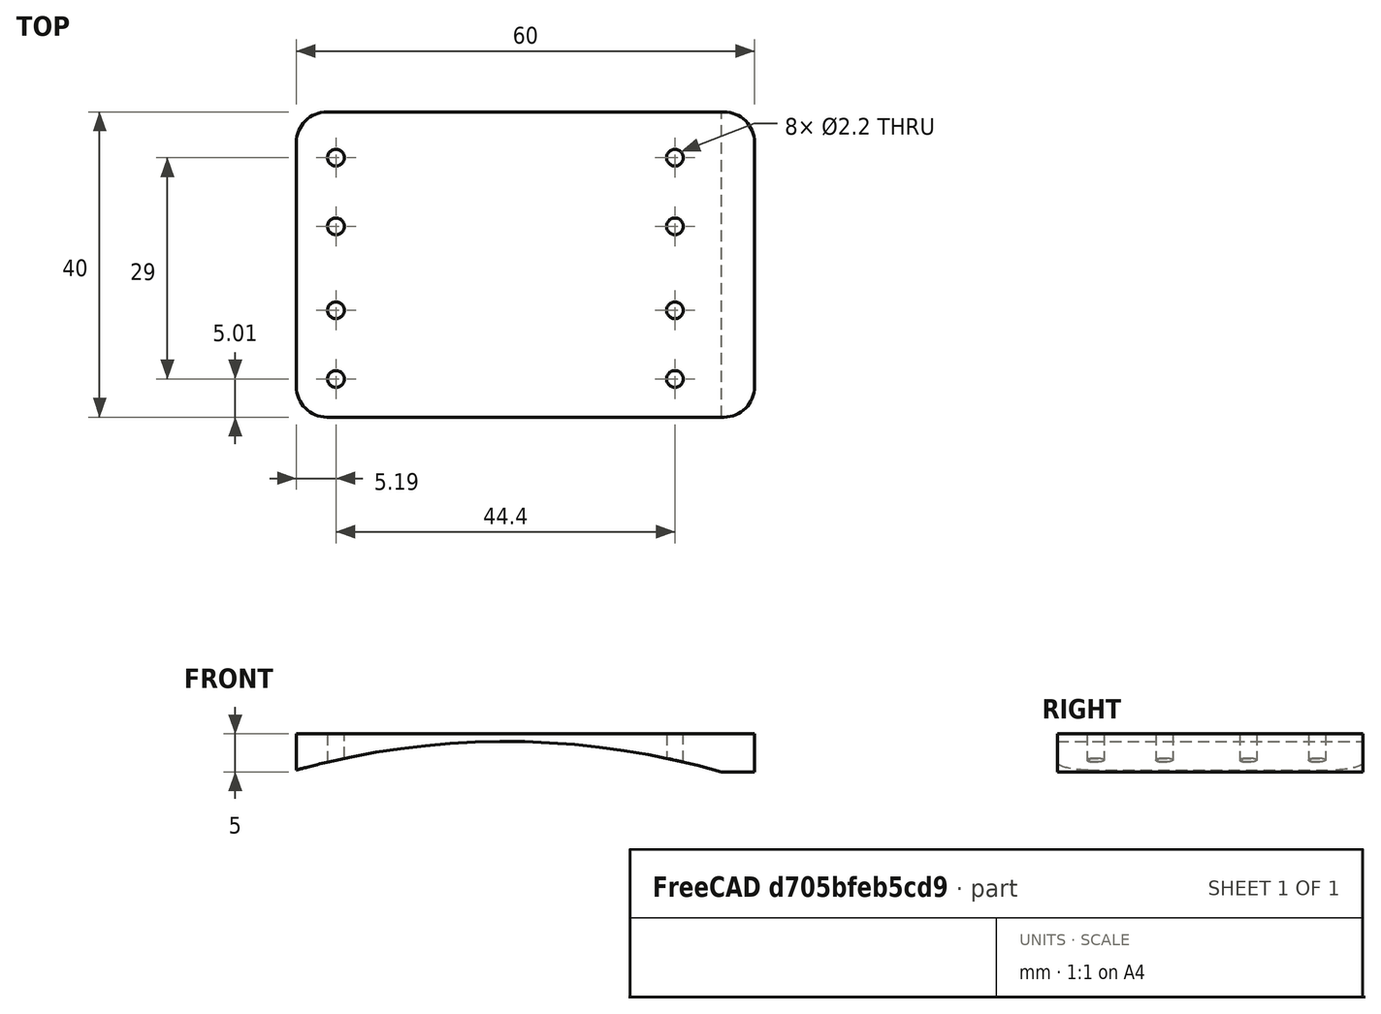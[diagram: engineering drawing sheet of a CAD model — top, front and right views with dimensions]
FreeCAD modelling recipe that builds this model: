
FCSTD DOCUMENT  (FreeCAD 1.0R38806 (Git))
Label: baseplate
License: All rights reserved
LicenseURL: http://en.wikipedia.org/wiki/All_rights_reserved
objects: Sketcher::SketchObject×2, PartDesign::Pad×1, Part::Cylinder×1, PartDesign::Pocket×1, PartDesign::Body×1, Part::Cut×1
note: 13 computed .brp shape members not serialized (recipe doc carries the construction recipe); baked Part::Feature solids carry a one-line shape summary decoded from their .brp

FEATURE [Sketcher::SketchObject] Sketch
  ArcFitTolerance = 0
  AttachmentSupport = -> [XY_Plane]
  FullyConstrained = false
  MakeInternals = false
  MapMode = 5
  sketch-geometry (8):
    g0: LineSegment StartX=0.614893 StartY=-1.00664 StartZ=0 EndX=52.6149 EndY=-1.00664 EndZ=0
    g1: LineSegment StartX=56.6149 StartY=2.99336 StartZ=0 EndX=56.6149 EndY=34.9934 EndZ=0
    g2: LineSegment StartX=52.6149 StartY=38.9934 StartZ=0 EndX=0.614893 EndY=38.9934 EndZ=0
    g3: LineSegment StartX=-3.38511 StartY=34.9934 StartZ=0 EndX=-3.38511 EndY=2.99336 EndZ=0
    g4: ArcOfCircle CenterX=52.6149 CenterY=34.9934 CenterZ=0 NormalX=0 NormalY=0 NormalZ=1 AngleXU=0 Radius=4 StartAngle=7e-16 EndAngle=1.5708
    g5: ArcOfCircle CenterX=52.6149 CenterY=2.99336 CenterZ=0 NormalX=0 NormalY=0 NormalZ=1 AngleXU=0 Radius=4 StartAngle=4.71239 EndAngle=6.28319
    g6: ArcOfCircle CenterX=0.614893 CenterY=2.99336 CenterZ=0 NormalX=0 NormalY=0 NormalZ=1 AngleXU=0 Radius=4 StartAngle=3.14159 EndAngle=4.71239
    g7: ArcOfCircle CenterX=0.614893 CenterY=34.9934 CenterZ=0 NormalX=0 NormalY=0 NormalZ=1 AngleXU=0 Radius=4 StartAngle=1.5708 EndAngle=3.14159
  constraints (18):
    c: Horizontal(g0)
    c: Horizontal(g2)
    c: Vertical(g1)
    c: Vertical(g3)
    c: Tangent(g2,g4) = -1.5708
    c: Tangent(g1,g4) = -1.5708
    c: Tangent(g1,g5) = -1.5708
    c: Tangent(g0,g5) = -1.5708
    c: Tangent(g0,g6) = -1.5708
    c: Tangent(g3,g6) = -1.5708
    c: Tangent(g3,g7) = -1.5708
    c: Tangent(g2,g7) = -1.5708
    c: Radius(g7) = 4
    c: Radius(g4) = 4
    c: Radius(g5) = 4
    c: Radius(g6) = 4
    c: DistanceY(g0,g2) = 40
    c: DistanceX(g3,g1) = 60
FEATURE [PartDesign::Pad] Pad
  Direction = (0,0,1)
  Length = 5
  Length2 = 10
  Profile = -> Sketch
  ReferenceAxis = -> Sketch [N_Axis]
  Refine = true
  Suppressed = false
  Type = 0
FEATURE [Part::Cylinder] Cylinder
  Angle = 360
  AttacherType = Attacher::AttachEngine3D
  FirstAngle = 0
  Height = 80
  Placement = pos=(24,50,-98) rot=(1,0,0;1.5708rad)
  Radius = 102
  SecondAngle = 0
FEATURE [Sketcher::SketchObject] Sketch008
  ArcFitTolerance = 0
  FullyConstrained = false
  MakeInternals = false
  MapMode = 5
  Placement = pos=(0,0,0) rot=(1,0,0;3.14159rad)
  sketch-geometry (8):
    g0: Circle CenterX=1.8 CenterY=-4 CenterZ=0 NormalX=0 NormalY=0 NormalZ=1 AngleXU=0 Radius=1.1
    g1: Circle CenterX=1.8 CenterY=-13 CenterZ=0 NormalX=0 NormalY=0 NormalZ=1 AngleXU=0 Radius=1.1
    g2: Circle CenterX=1.8 CenterY=-24 CenterZ=0 NormalX=0 NormalY=0 NormalZ=1 AngleXU=0 Radius=1.1
    g3: Circle CenterX=1.8 CenterY=-33 CenterZ=0 NormalX=0 NormalY=0 NormalZ=1 AngleXU=0 Radius=1.1
    g4: Circle CenterX=46.2 CenterY=-4 CenterZ=0 NormalX=0 NormalY=0 NormalZ=1 AngleXU=0 Radius=1.1
    g5: Circle CenterX=46.2 CenterY=-13 CenterZ=0 NormalX=0 NormalY=0 NormalZ=1 AngleXU=0 Radius=1.1
    g6: Circle CenterX=46.2 CenterY=-24 CenterZ=0 NormalX=0 NormalY=0 NormalZ=1 AngleXU=0 Radius=1.1
    g7: Circle CenterX=46.2 CenterY=-33 CenterZ=0 NormalX=0 NormalY=0 NormalZ=1 AngleXU=0 Radius=1.1
FEATURE [PartDesign::Pocket] Pocket
  BaseFeature = -> Pad
  Direction = (0,1e-16,1)
  Length = 8
  Length2 = 5
  Profile = -> Sketch008
  ReferenceAxis = -> Sketch008 [N_Axis]
  Refine = true
  Suppressed = false
  Type = 0
FEATURE [PartDesign::Body] Body
  AllowCompound = false
  Group = -> [Sketch,Pad,Sketch008,Pocket]
  Origin = -> Origin
  Tip = -> Pocket
FEATURE [Part::Cut] Cut
  Base = -> Body
  Refine = true
  Tool = -> Cylinder
